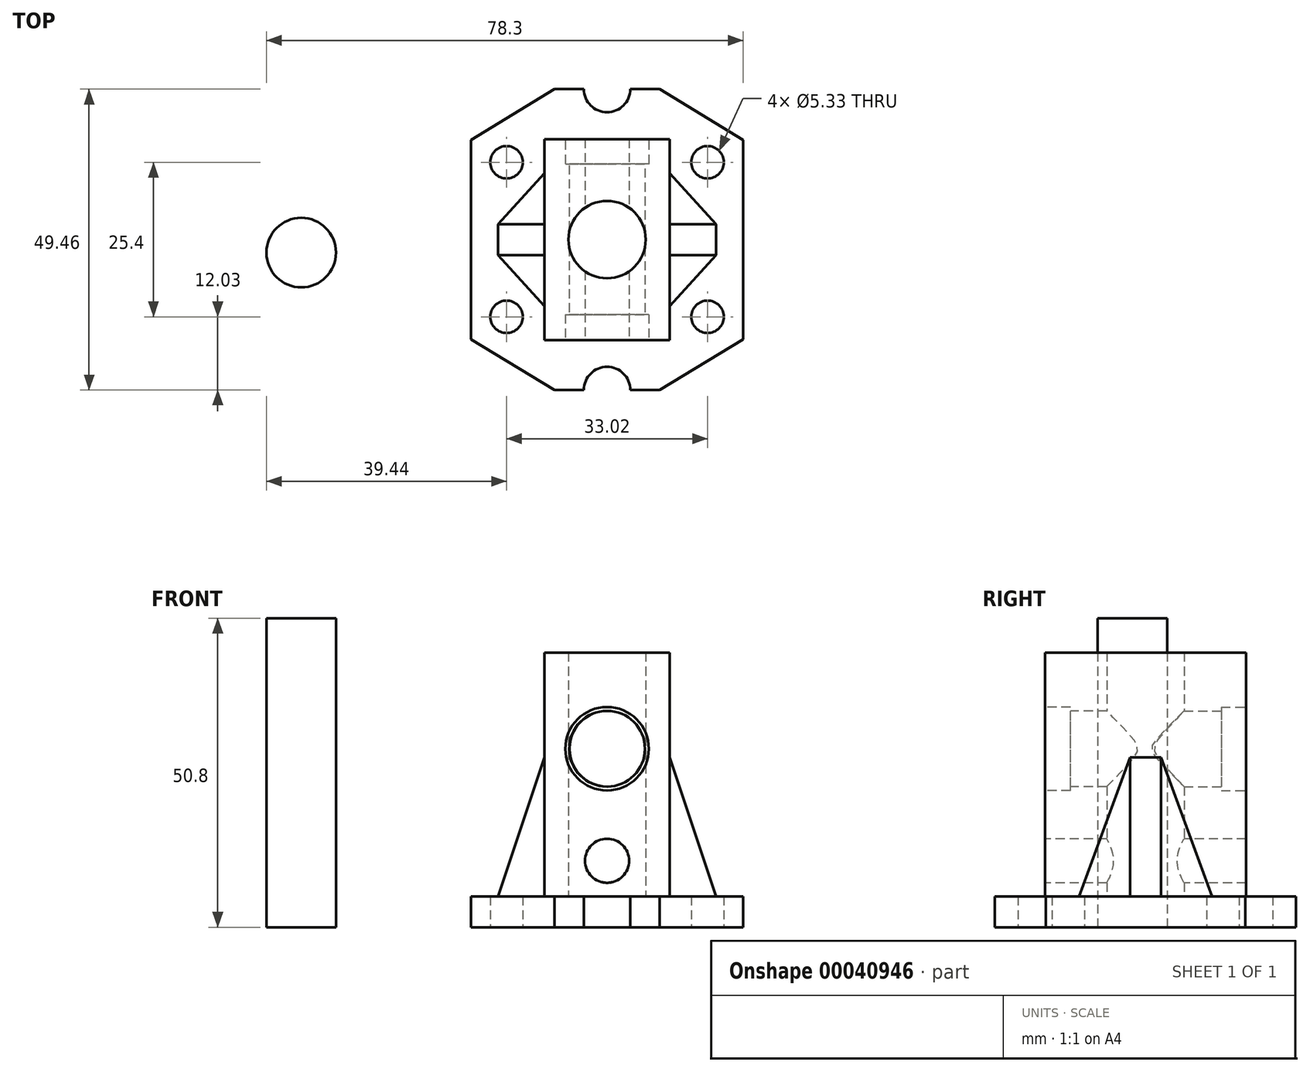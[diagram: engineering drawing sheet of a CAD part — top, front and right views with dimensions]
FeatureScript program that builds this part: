
annotation { "Feature Type Name" : "Feature", "Feature Type Description" : "" }
export const myFeature = defineFeature(function(context is Context, id is Id, definition is map)
    precondition{}
    {
        {
            var Q0;
            Q0=qCreatedBy(makeId("Top.planeOp"),FACE);
            var sketch = newSketch(context, id + "F0", { "sketchPlane" : qUnion([Q0])});
            skPoint(sketch, "E0.rect.middle", {"position": v(0, 0) * mm});
            skLineSegment(sketch, "E1", {"start": v(-22.35, 0) * mm, "end": v(-22.35, 16.38) * mm});
            skLineSegment(sketch, "E2", {"start": v(-22.35, 16.38) * mm, "end": v(-8.64, 24.73) * mm});
            skLineSegment(sketch, "E3", {"start": v(-8.64, 24.73) * mm, "end": v(-3.81, 24.73) * mm});
            skLineSegment(sketch, "E4.MirrorCS", {"start": v(22.35, 0) * mm, "end": v(22.35, 16.38) * mm});
            skLineSegment(sketch, "E5.MirrorCS", {"start": v(8.64, 24.73) * mm, "end": v(3.81, 24.73) * mm});
            skLineSegment(sketch, "E6.MirrorCS", {"start": v(22.35, 16.38) * mm, "end": v(8.64, 24.73) * mm});
            skLineSegment(sketch, "E7.MirrorCS", {"start": v(22.35, -16.38) * mm, "end": v(8.64, -24.73) * mm});
            skLineSegment(sketch, "E8.MirrorCS", {"start": v(8.64, -24.73) * mm, "end": v(0, -24.73) * mm});
            skLineSegment(sketch, "E9.MirrorCS", {"start": v(22.35, 0) * mm, "end": v(22.35, -16.38) * mm});
            skLineSegment(sketch, "E10.MirrorCS", {"start": v(-8.64, -24.73) * mm, "end": v(0, -24.73) * mm});
            skLineSegment(sketch, "E11.MirrorCS", {"start": v(-22.35, 0) * mm, "end": v(-22.35, -16.38) * mm});
            skLineSegment(sketch, "E12.MirrorCS", {"start": v(-22.35, -16.38) * mm, "end": v(-8.64, -24.73) * mm});
            skLineSegment(sketch, "E13", {"start": v(-8.64, 24.73) * mm, "end": v(-8.64, -24.73) * mm});
            skLineSegment(sketch, "E14", {"start": v(-22.35, 16.38) * mm, "end": v(22.35, 16.38) * mm});
            skLineSegment(sketch, "E15", {"start": v(-16.51, 0) * mm, "end": v(-16.51, 12.7) * mm});
            skLineSegment(sketch, "E16", {"start": v(-22.35, 12.7) * mm, "end": v(-16.51, 12.7) * mm});
            skCircle(sketch, "E17", {"center": v(-16.51, 12.7) * mm, "radius": 2.67 * mm});
            skCircle(sketch, "E18.MirrorC", {"center": v(-16.51, -12.7) * mm, "radius": 2.67 * mm});
            skCircle(sketch, "E19.MirrorC", {"center": v(16.51, -12.7) * mm, "radius": 2.67 * mm});
            skCircle(sketch, "E20.MirrorC", {"center": v(16.51, 12.7) * mm, "radius": 2.67 * mm});
            skArc(sketch, "E21", {"start": v(-3.81, 24.73) * mm, "mid": v(0, 20.92) * mm, "end": v(3.81, 24.73) * mm});
            skCircle(sketch, "E22.MirrorC", {"center": v(0, -24.73) * mm, "radius": 3.81 * mm});
            skSolve(sketch);
        }
        {
            var Q0;
            {var subQ9=sQuery(id+"F0.wireOp",EDGE,"E11.MirrorCS");Q0=makeQuery(id+"F0.imprint","IMPRINT",FACE,{"disambiguationData":[TD([[makeQuery(id+"F0.imprint","IMPRINT",EDGE,{"derivedFrom":subQ9}),1.0]])]});}
            var Q1;
            {var subQ7=sQuery(id+"F0.wireOp",EDGE,"E4.MirrorCS");Q1=makeQuery(id+"F0.imprint","IMPRINT",FACE,{"disambiguationData":[TD([[makeQuery(id+"F0.imprint","IMPRINT",EDGE,{"derivedFrom":subQ7}),1.0]])]});}
            var Q2;
            {var subQ4=sQuery(id+"F0.wireOp",EDGE,"E3");Q2=makeQuery(id+"F0.imprint","IMPRINT",FACE,{"disambiguationData":[TD([[makeQuery(id+"F0.imprint","IMPRINT",EDGE,{"derivedFrom":subQ4}),-1.0]])]});}
            var Q3;
            {var subQ3=sQuery(id+"F0.wireOp",EDGE,"E2");Q3=makeQuery(id+"F0.imprint","IMPRINT",FACE,{"disambiguationData":[TD([[makeQuery(id+"F0.imprint","IMPRINT",EDGE,{"derivedFrom":subQ3}),-1.0]])]});}
            extrude(context, id + "F1", {"entities" : qUnion([Q0, Q1, Q2, Q3]), "depth" : 5.08 * mm});
        }
        {
            var Q0;
            Q0=makeQuery(id+"F1.opExtrude","CAP_FACE",FACE,{"disambiguationData":[OSD([sQuery(id+"F0.wireOp",EDGE,"E1"),sQuery(id+"F0.wireOp",EDGE,"E2"),sQuery(id+"F0.wireOp",EDGE,"E3"),sQuery(id+"F0.wireOp",EDGE,"E4.MirrorCS"),sQuery(id+"F0.wireOp",EDGE,"E5.MirrorCS"),sQuery(id+"F0.wireOp",EDGE,"E6.MirrorCS"),sQuery(id+"F0.wireOp",EDGE,"E7.MirrorCS"),sQuery(id+"F0.wireOp",EDGE,"E8.MirrorCS"),sQuery(id+"F0.wireOp",EDGE,"E9.MirrorCS"),sQuery(id+"F0.wireOp",EDGE,"E10.MirrorCS"),sQuery(id+"F0.wireOp",EDGE,"E11.MirrorCS"),sQuery(id+"F0.wireOp",EDGE,"E12.MirrorCS"),sQuery(id+"F0.wireOp",EDGE,"E17"),sQuery(id+"F0.wireOp",EDGE,"E18.MirrorC"),sQuery(id+"F0.wireOp",EDGE,"E19.MirrorC"),sQuery(id+"F0.wireOp",EDGE,"E20.MirrorC"),sQuery(id+"F0.wireOp",EDGE,"E21"),sQuery(id+"F0.wireOp",EDGE,"E22.MirrorC")])],"isStart":false});
            var sketch = newSketch(context, id + "F2", { "sketchPlane" : qUnion([Q0])});
            skLineSegment(sketch, "E23.rect.bottom", {"start": v(10.29, -16.51) * mm, "end": v(-10.29, -16.51) * mm});
            skLineSegment(sketch, "E23.rect.top", {"start": v(10.29, 16.51) * mm, "end": v(-10.29, 16.51) * mm});
            skLineSegment(sketch, "E23.rect.left", {"start": v(10.29, -16.51) * mm, "end": v(10.29, 16.51) * mm});
            skLineSegment(sketch, "E23.rect.right", {"start": v(-10.29, -16.51) * mm, "end": v(-10.29, 16.51) * mm});
            skPoint(sketch, "E23.rect.middle", {"position": v(0, 0) * mm});
            skSolve(sketch);
        }
        {
            var Q0;
            Q0=makeQuery(id+"F2.imprint","IMPRINT",FACE,{"disambiguationData":[TD([[makeQuery(id+"F2.imprint","IMPRINT",EDGE,{"derivedFrom":sQuery(id+"F2.wireOp",EDGE,"E23.rect.bottom")}),-1.0]])]});
            extrude(context, id + "F3", {"entities" : qUnion([Q0]), "depth" : 40.06 * mm});
        }
        {
            var Q0;
            Q0=makeQuery(id+"F3.opExtrude","SWEPT_FACE",FACE,{"disambiguationData":[OSD([sQuery(id+"F2.wireOp",EDGE,"E23.rect.right")])]});
            var sketch = newSketch(context, id + "F4", { "sketchPlane" : qUnion([Q0])});
            skLineSegment(sketch, "E24", {"start": v(0, 5.08) * mm, "end": v(2.54, 5.08) * mm});
            skLineSegment(sketch, "E25", {"start": v(2.54, 5.08) * mm, "end": v(10.92, 5.08) * mm});
            skLineSegment(sketch, "E26", {"start": v(10.92, 5.08) * mm, "end": v(2.54, 27.94) * mm});
            skLineSegment(sketch, "E27", {"start": v(2.54, 27.94) * mm, "end": v(0, 27.94) * mm});
            skLineSegment(sketch, "E28.MirrorCS", {"start": v(-2.54, 27.94) * mm, "end": v(0, 27.94) * mm});
            skLineSegment(sketch, "E29.MirrorCS", {"start": v(-10.92, 5.08) * mm, "end": v(-2.54, 27.94) * mm});
            skLineSegment(sketch, "E30.MirrorCS", {"start": v(-2.54, 5.08) * mm, "end": v(-10.92, 5.08) * mm});
            skLineSegment(sketch, "E31.MirrorCS", {"start": v(0, 5.08) * mm, "end": v(-2.54, 5.08) * mm});
            skLineSegment(sketch, "E32", {"start": v(-2.54, 27.94) * mm, "end": v(-2.54, 5.08) * mm});
            skLineSegment(sketch, "E33", {"start": v(2.54, 5.08) * mm, "end": v(2.54, 27.94) * mm});
            skSolve(sketch);
        }
        {
            var Q0;
            Q0=makeQuery(id+"F3.opExtrude","SWEPT_FACE",FACE,{"disambiguationData":[OSD([sQuery(id+"F2.wireOp",EDGE,"E23.rect.top")])]});
            var Q1;
            Q1=makeQuery(id+"F3.opExtrude","SWEPT_FACE",FACE,{"disambiguationData":[OSD([sQuery(id+"F2.wireOp",EDGE,"E23.rect.bottom")])]});
            cPlane(context, id + "F5", {"entities" : qUnion([Q0, Q1]), "cplaneType" : CPlaneType.MID_PLANE, "offset" : 152.4 * mm, "width" : 152.4 * mm, "height" : 152.4 * mm});
        }
        {
            var Q0;
            Q0=qCreatedBy(id+"F5.planeOp",FACE);
            var sketch = newSketch(context, id + "F6", { "sketchPlane" : qUnion([Q0])});
            skLineSegment(sketch, "E34", {"start": v(10.29, 27.94) * mm, "end": v(10.29, 5.08) * mm});
            skLineSegment(sketch, "E35", {"start": v(10.29, 5.08) * mm, "end": v(17.9, 5.08) * mm});
            skLineSegment(sketch, "E36", {"start": v(17.9, 5.08) * mm, "end": v(10.29, 27.94) * mm});
            skSolve(sketch);
        }
        {
            var Q0;
            Q0=makeQuery(id+"F6.imprint","IMPRINT",FACE,{"disambiguationData":[TD([[makeQuery(id+"F6.imprint","IMPRINT",EDGE,{"derivedFrom":sQuery(id+"F6.wireOp",EDGE,"E34")}),1.0]])]});
            extrude(context, id + "F7", {"entities" : qUnion([Q0]), "depth" : 5.08 * mm, "symmetric" : true});
        }
        {
            var Q0;
            Q0=sQuery(id+"F4.wireOp",EDGE,"E29.MirrorCS");
            var Q1;
            Q1=makeQuery(id+"F7.opExtrude","CAP_EDGE",EDGE,{"disambiguationData":[OSD([sQuery(id+"F6.wireOp",EDGE,"E36")])],"isStart":false});
            cPlane(context, id + "F8", {"entities" : qUnion([Q0, Q1]), "cplaneType" : CPlaneType.LINE_ANGLE, "offset" : 152.4 * mm, "angle" : 0 * degree, "width" : 152.4 * mm, "height" : 152.4 * mm});
        }
        {
            var Q0;
            Q0=makeQuery(id+"F4.imprint","IMPRINT",FACE,{"disambiguationData":[TD([[makeQuery(id+"F4.imprint","IMPRINT",EDGE,{"derivedFrom":sQuery(id+"F4.wireOp",EDGE,"E29.MirrorCS")}),-1.0]])]});
            var Q1;
            Q1=qCreatedBy(id+"F8.planeOp",FACE);
            extrude(context, id + "F9", {"entities" : qUnion([Q0]), "endBound" : BoundingType.UP_TO_SURFACE, "endBoundEntityFace" : qUnion([Q1]), "depth" : 25.4 * mm});
        }
        {
            var Q0;
            Q0=makeQuery(id+"F9.opExtrude","SWEPT_BODY",BODY,{"disambiguationData":[OSD([sQuery(id+"F4.wireOp",EDGE,"E29.MirrorCS"),sQuery(id+"F4.wireOp",EDGE,"E30.MirrorCS"),sQuery(id+"F4.wireOp",EDGE,"E32")])]});
            var Q1;
            Q1=qCreatedBy(id+"F5.planeOp",FACE);
            mirror(context, id + "F10", {"entities" : qUnion([Q0]), "mirrorPlane" : qUnion([Q1])});
        }
        {
            var Q0;
            Q0=makeQuery(id+"F9.opExtrude","SWEPT_BODY",BODY,{"disambiguationData":[OSD([sQuery(id+"F4.wireOp",EDGE,"E29.MirrorCS"),sQuery(id+"F4.wireOp",EDGE,"E30.MirrorCS"),sQuery(id+"F4.wireOp",EDGE,"E32")])]});
            var Q1;
            Q1=makeQuery(id+"F7.opExtrude","SWEPT_BODY",BODY,{"disambiguationData":[OSD([sQuery(id+"F6.wireOp",EDGE,"E34"),sQuery(id+"F6.wireOp",EDGE,"E35"),sQuery(id+"F6.wireOp",EDGE,"E36")])]});
            var Q2;
            Q2=makeQuery(id+"F10.opPattern","COPY",BODY,{"derivedFrom":makeQuery(id+"F9.opExtrude","SWEPT_BODY",BODY,{"disambiguationData":[OSD([sQuery(id+"F4.wireOp",EDGE,"E29.MirrorCS"),sQuery(id+"F4.wireOp",EDGE,"E30.MirrorCS"),sQuery(id+"F4.wireOp",EDGE,"E32")])]}),"instanceName":"1"});
            var Q3;
            Q3=qCreatedBy(makeId("Right.planeOp"),FACE);
            mirror(context, id + "F11", {"entities" : qUnion([Q0, Q1, Q2]), "mirrorPlane" : qUnion([Q3])});
        }
        {
            var Q0;
            Q0=makeQuery(id+"F3.opExtrude","SWEPT_FACE",FACE,{"disambiguationData":[OSD([sQuery(id+"F2.wireOp",EDGE,"E23.rect.bottom")])]});
            var sketch = newSketch(context, id + "F12", { "sketchPlane" : qUnion([Q0])});
            skLineSegment(sketch, "E37", {"start": v(0, 5.08) * mm, "end": v(0, 10.92) * mm});
            skPoint(sketch, "E37.endSnap0", {"position": v(0, 5.08) * mm});
            skCircle(sketch, "E38", {"center": v(0, 10.92) * mm, "radius": 3.62 * mm});
            skCircle(sketch, "E39", {"center": v(0, 29.34) * mm, "radius": 6.22 * mm});
            skCircle(sketch, "E40", {"center": v(0, 29.34) * mm, "radius": 6.86 * mm});
            skLineSegment(sketch, "E41", {"start": v(0, 5.08) * mm, "end": v(0, 22.48) * mm});
            skSolve(sketch);
        }
        {
            var Q0;
            Q0=makeQuery(id+"F12.imprint","IMPRINT",FACE,{"disambiguationData":[TD([[makeQuery(id+"F12.imprint","IMPRINT",EDGE,{"derivedFrom":sQuery(id+"F12.wireOp",EDGE,"E39")}),1.0]])]});
            var Q1;
            Q1=qCreatedBy(makeId("Front.planeOp"),FACE);
            extrude(context, id + "F13", {"entities" : qUnion([Q0]), "operationType" : NewBodyOperationType.REMOVE, "endBound" : BoundingType.UP_TO_SURFACE, "oppositeDirection" : true, "endBoundEntityFace" : qUnion([Q1]), "depth" : 25.4 * mm});
        }
        {
            var Q0;
            Q0=makeQuery(id+"F12.imprint","IMPRINT",FACE,{"disambiguationData":[TD([[makeQuery(id+"F12.imprint","IMPRINT",EDGE,{"derivedFrom":sQuery(id+"F12.wireOp",EDGE,"E39")}),-1.0]])]});
            var Q1;
            Q1=sQuery(id+"F12.wireOp",EDGE,"E40");
            extrude(context, id + "F14", {"entities" : qUnion([Q0]), "operationType" : NewBodyOperationType.REMOVE, "surfaceEntities" : qUnion([Q1]), "oppositeDirection" : true, "depth" : 4.2 * mm});
        }
        {
            var Q0;
            Q0=makeQuery(id+"F3.opExtrude","SWEPT_FACE",FACE,{"disambiguationData":[OSD([sQuery(id+"F2.wireOp",EDGE,"E23.rect.top")])]});
            var sketch = newSketch(context, id + "F15", { "sketchPlane" : qUnion([Q0])});
            skLineSegment(sketch, "E42", {"start": v(-0.05, 5.08) * mm, "end": v(-0.05, 10.92) * mm});
            skPoint(sketch, "E42.endSnap0", {"position": v(-0.05, 5.08) * mm});
            skCircle(sketch, "E43", {"center": v(-0.05, 10.92) * mm, "radius": 3.62 * mm});
            skCircle(sketch, "E44", {"center": v(-0.05, 29.34) * mm, "radius": 6.22 * mm});
            skCircle(sketch, "E45", {"center": v(-0.05, 29.34) * mm, "radius": 6.86 * mm});
            skLineSegment(sketch, "E46", {"start": v(-0.05, 5.08) * mm, "end": v(-0.05, 22.48) * mm});
            skSolve(sketch);
        }
        {
            var Q0;
            Q0=makeQuery(id+"F15.imprint","IMPRINT",FACE,{"disambiguationData":[TD([[makeQuery(id+"F15.imprint","IMPRINT",EDGE,{"derivedFrom":sQuery(id+"F15.wireOp",EDGE,"E45")}),1.0]])]});
            var Q1;
            Q1=sQuery(id+"F15.wireOp",EDGE,"E45");
            extrude(context, id + "F16", {"entities" : qUnion([Q0]), "operationType" : NewBodyOperationType.REMOVE, "surfaceEntities" : qUnion([Q1]), "oppositeDirection" : true, "depth" : 4.06 * mm});
        }
        {
            var Q0;
            Q0=makeQuery(id+"F15.imprint","IMPRINT",FACE,{"disambiguationData":[TD([[makeQuery(id+"F15.imprint","IMPRINT",EDGE,{"derivedFrom":sQuery(id+"F15.wireOp",EDGE,"E44")}),1.0]])]});
            var Q1;
            Q1=qCreatedBy(makeId("Front.planeOp"),FACE);
            extrude(context, id + "F17", {"entities" : qUnion([Q0]), "operationType" : NewBodyOperationType.REMOVE, "endBound" : BoundingType.UP_TO_SURFACE, "oppositeDirection" : true, "endBoundEntityFace" : qUnion([Q1]), "depth" : 25.4 * mm});
        }
        {
            var Q0;
            {var subQ0=sQuery(id+"F12.wireOp",EDGE,"E41");var subQ3=makeQuery(id+"F12.imprint","IMPRINT",VERTEX,{"derivedFrom":subQ0});Q0=makeQuery(id+"F12.imprint","IMPRINT",FACE,{"disambiguationData":[TD([[makeQuery(id+"F12.imprint","IMPRINT",EDGE,{"disambiguationData":[TD([[subQ3,1.0]])],"derivedFrom":subQ0}),-1.0]])]});}
            var Q1;
            {var subQ0=sQuery(id+"F12.wireOp",EDGE,"E41");var subQ3=makeQuery(id+"F12.imprint","IMPRINT",VERTEX,{"derivedFrom":subQ0});Q1=makeQuery(id+"F12.imprint","IMPRINT",FACE,{"disambiguationData":[TD([[makeQuery(id+"F12.imprint","IMPRINT",EDGE,{"disambiguationData":[TD([[subQ3,1.0]])],"derivedFrom":subQ0}),1.0]])]});}
            extrude(context, id + "F18", {"entities" : qUnion([Q0, Q1]), "operationType" : NewBodyOperationType.REMOVE, "endBound" : BoundingType.THROUGH_ALL, "oppositeDirection" : true, "depth" : 25.4 * mm});
        }
        {
            var Q0;
            Q0=makeQuery(id+"F3.opExtrude","CAP_FACE",FACE,{"disambiguationData":[OSD([sQuery(id+"F2.wireOp",EDGE,"E23.rect.bottom"),sQuery(id+"F2.wireOp",EDGE,"E23.rect.top"),sQuery(id+"F2.wireOp",EDGE,"E23.rect.left"),sQuery(id+"F2.wireOp",EDGE,"E23.rect.right")])],"isStart":false});
            var sketch = newSketch(context, id + "F19", { "sketchPlane" : qUnion([Q0])});
            skPoint(sketch, "E47", {"position": v(0, 0) * mm});
            skSolve(sketch);
        }
        {
            var Q0;
            Q0=sQuery(id+"F19.wireOp",VERTEX,"E47");
            var Q1;
            Q1=makeQuery(id+"F3.opExtrude","SWEPT_BODY",BODY,{"disambiguationData":[OSD([sQuery(id+"F2.wireOp",EDGE,"E23.rect.bottom"),sQuery(id+"F2.wireOp",EDGE,"E23.rect.top"),sQuery(id+"F2.wireOp",EDGE,"E23.rect.left"),sQuery(id+"F2.wireOp",EDGE,"E23.rect.right")])]});
            hole(context, id + "F20", {"style" : HoleStyle.SIMPLE, "holeDiameter" : 12.7 * mm, "endStyle" : HoleEndStyle.BLIND, "holeDepth" : 41.9 * mm, "locations" : qUnion([Q0]), "scope" : qUnion([Q1])});
        }
        {
            var Q0;
            Q0=qCreatedBy(makeId("Top.planeOp"),FACE);
            var sketch = newSketch(context, id + "F21", { "sketchPlane" : qUnion([Q0])});
            skCircle(sketch, "E48", {"center": v(-50.24, -2.15) * mm, "radius": 5.72 * mm});
            skSolve(sketch);
        }
        {
            var Q0;
            Q0=makeQuery(id+"F21.imprint","IMPRINT",FACE,{"disambiguationData":[TD([[makeQuery(id+"F21.imprint","IMPRINT",EDGE,{"derivedFrom":sQuery(id+"F21.wireOp",EDGE,"E48")}),1.0]])]});
            var Q1;
            Q1=sQuery(id+"F21.wireOp",EDGE,"E48");
            extrude(context, id + "F22", {"entities" : qUnion([Q0]), "surfaceEntities" : qUnion([Q1]), "depth" : 50.8 * mm});
        }
    });
